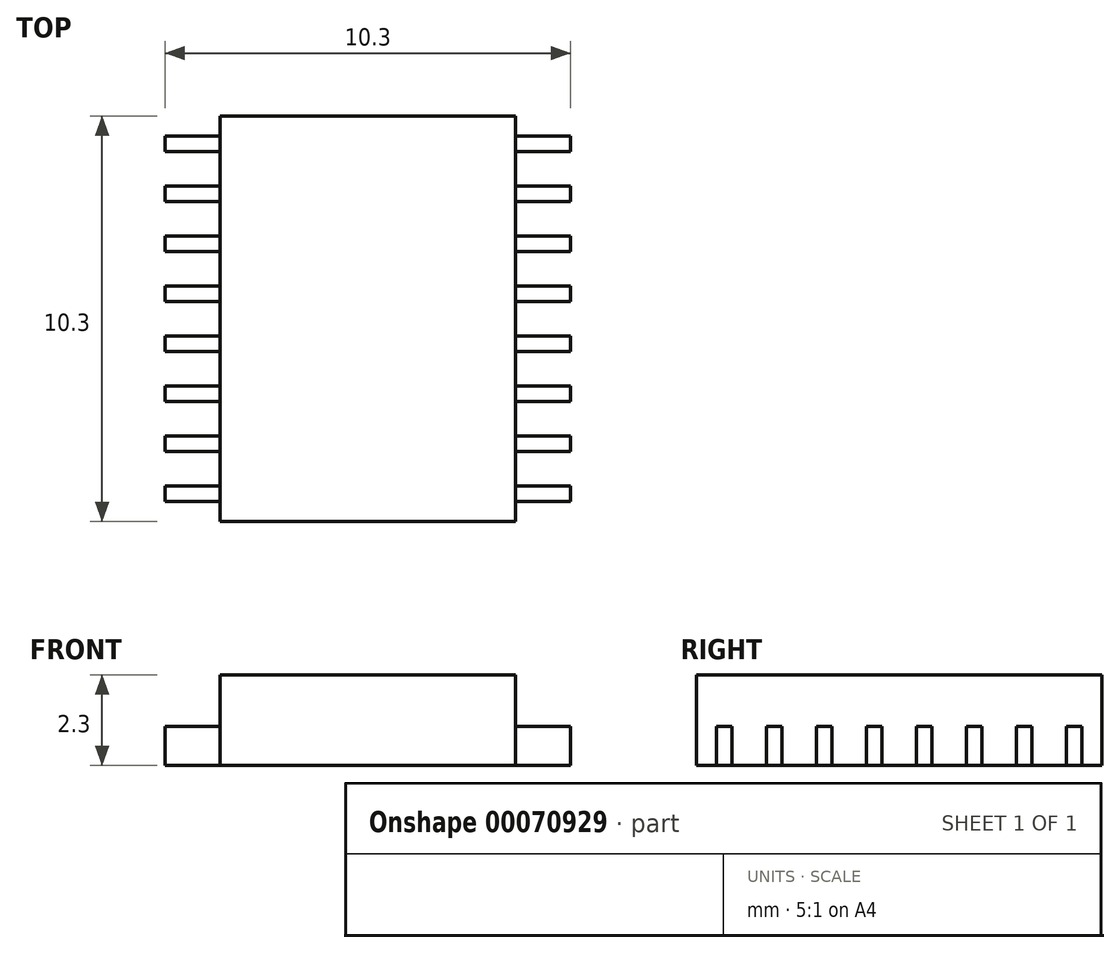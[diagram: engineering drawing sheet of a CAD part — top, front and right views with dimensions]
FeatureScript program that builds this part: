
annotation { "Feature Type Name" : "Feature", "Feature Type Description" : "" }
export const myFeature = defineFeature(function(context is Context, id is Id, definition is map)
    precondition{}
    {
        {
            var Q0;
            Q0=qCreatedBy(makeId("Top.planeOp"),FACE);
            var sketch = newSketch(context, id + "F0", { "sketchPlane" : qUnion([Q0])});
            skLineSegment(sketch, "E0.rect.bottom", {"start": v(3.75, -5.15) * mm, "end": v(-3.75, -5.15) * mm});
            skLineSegment(sketch, "E0.rect.top", {"start": v(3.75, 5.15) * mm, "end": v(-3.75, 5.15) * mm});
            skLineSegment(sketch, "E0.rect.left", {"start": v(3.75, -5.15) * mm, "end": v(3.75, 5.15) * mm});
            skLineSegment(sketch, "E0.rect.right", {"start": v(-3.75, -5.15) * mm, "end": v(-3.75, 5.15) * mm});
            skPoint(sketch, "E0.rect.middle", {"position": v(0, 0) * mm});
            skSolve(sketch);
        }
        {
            var Q0;
            Q0=qSketchRegion(id+"F0",true);
            extrude(context, id + "F1", {"entities" : qUnion([Q0]), "depth" : 2.3 * mm});
        }
        {
            var Q0;
            Q0=qCreatedBy(makeId("Top.planeOp"),FACE);
            var sketch = newSketch(context, id + "F2", { "sketchPlane" : qUnion([Q0])});
            skLineSegment(sketch, "E1.bottom", {"start": v(-3.75, 4.65) * mm, "end": v(-5.15, 4.65) * mm});
            skLineSegment(sketch, "E1.top", {"start": v(-3.75, 4.25) * mm, "end": v(-5.15, 4.25) * mm});
            skLineSegment(sketch, "E1.left", {"start": v(-3.75, 4.65) * mm, "end": v(-3.75, 4.25) * mm});
            skLineSegment(sketch, "E1.right", {"start": v(-5.15, 4.65) * mm, "end": v(-5.15, 4.25) * mm});
            skLineSegment(sketch, "E2.bottom", {"start": v(-5.15, 3.38) * mm, "end": v(-3.75, 3.38) * mm});
            skLineSegment(sketch, "E2.top", {"start": v(-5.15, 2.98) * mm, "end": v(-3.75, 2.98) * mm});
            skLineSegment(sketch, "E2.left", {"start": v(-5.15, 3.38) * mm, "end": v(-5.15, 2.98) * mm});
            skLineSegment(sketch, "E2.right", {"start": v(-3.75, 3.38) * mm, "end": v(-3.75, 2.98) * mm});
            skLineSegment(sketch, "E3.bottom", {"start": v(-5.15, 2.1) * mm, "end": v(-3.75, 2.1) * mm});
            skLineSegment(sketch, "E3.top", {"start": v(-5.15, 1.7) * mm, "end": v(-3.75, 1.7) * mm});
            skLineSegment(sketch, "E3.left", {"start": v(-5.15, 2.1) * mm, "end": v(-5.15, 1.7) * mm});
            skLineSegment(sketch, "E3.right", {"start": v(-3.75, 2.1) * mm, "end": v(-3.75, 1.7) * mm});
            skLineSegment(sketch, "E4.bottom", {"start": v(-5.15, -1.7) * mm, "end": v(-3.75, -1.7) * mm});
            skLineSegment(sketch, "E4.top", {"start": v(-5.15, -2.1) * mm, "end": v(-3.75, -2.1) * mm});
            skLineSegment(sketch, "E4.left", {"start": v(-5.15, -1.7) * mm, "end": v(-5.15, -2.1) * mm});
            skLineSegment(sketch, "E4.right", {"start": v(-3.75, -1.7) * mm, "end": v(-3.75, -2.1) * mm});
            skLineSegment(sketch, "E5.bottom", {"start": v(-5.15, 0.84) * mm, "end": v(-3.75, 0.84) * mm});
            skLineSegment(sketch, "E5.top", {"start": v(-5.15, 0.44) * mm, "end": v(-3.75, 0.44) * mm});
            skLineSegment(sketch, "E5.left", {"start": v(-5.15, 0.84) * mm, "end": v(-5.15, 0.43) * mm});
            skLineSegment(sketch, "E5.right", {"start": v(-3.75, 0.84) * mm, "end": v(-3.75, 0.44) * mm});
            skLineSegment(sketch, "E6.bottom", {"start": v(-5.15, -0.43) * mm, "end": v(-3.75, -0.43) * mm});
            skLineSegment(sketch, "E6.top", {"start": v(-5.15, -0.84) * mm, "end": v(-3.75, -0.84) * mm});
            skLineSegment(sketch, "E6.left", {"start": v(-5.15, -0.43) * mm, "end": v(-5.15, -0.84) * mm});
            skLineSegment(sketch, "E6.right", {"start": v(-3.75, -0.43) * mm, "end": v(-3.75, -0.83) * mm});
            skLineSegment(sketch, "E7.bottom", {"start": v(-5.15, -2.98) * mm, "end": v(-3.75, -2.98) * mm});
            skLineSegment(sketch, "E7.top", {"start": v(-5.15, -3.38) * mm, "end": v(-3.75, -3.38) * mm});
            skLineSegment(sketch, "E7.left", {"start": v(-5.15, -2.98) * mm, "end": v(-5.15, -3.38) * mm});
            skLineSegment(sketch, "E7.right", {"start": v(-3.75, -2.98) * mm, "end": v(-3.75, -3.38) * mm});
            skLineSegment(sketch, "E8.bottom", {"start": v(-5.15, -4.25) * mm, "end": v(-3.75, -4.25) * mm});
            skLineSegment(sketch, "E8.top", {"start": v(-5.15, -4.65) * mm, "end": v(-3.75, -4.65) * mm});
            skLineSegment(sketch, "E8.left", {"start": v(-5.15, -4.25) * mm, "end": v(-5.15, -4.65) * mm});
            skLineSegment(sketch, "E8.right", {"start": v(-3.75, -4.25) * mm, "end": v(-3.75, -4.64) * mm});
            skSolve(sketch);
        }
        {
            var Q0;
            Q0=qSketchRegion(id+"F2",true);
            extrude(context, id + "F3", {"entities" : qUnion([Q0]), "operationType" : NewBodyOperationType.ADD, "depth" : 1 * mm});
        }
        {
            var Q0;
            Q0=qCreatedBy(makeId("Front.planeOp"),FACE);
            var sketch = newSketch(context, id + "F4", { "sketchPlane" : qUnion([Q0])});
            skLineSegment(sketch, "E9", {"start": v(0, 0) * mm, "end": v(0, 9.6) * mm, "construction": true});
            skSolve(sketch);
        }
        {
            var Q0;
            Q0=makeQuery(id+"F1.opExtrude","SWEPT_BODY",BODY,{"disambiguationData":[OSD([sQuery(id+"F0.wireOp",EDGE,"E0.rect.bottom"),sQuery(id+"F0.wireOp",EDGE,"E0.rect.top"),sQuery(id+"F0.wireOp",EDGE,"E0.rect.left"),sQuery(id+"F0.wireOp",EDGE,"E0.rect.right")])]});
            var Q1;
            Q1=sQuery(id+"F4.wireOp",EDGE,"E9");
            circularPattern(context, id + "F5", {"operationType" : NewBodyOperationType.ADD, "entities" : qUnion([Q0]), "axis" : qUnion([Q1]), "angle" : 180 * degree, "instanceCount" : 2});
        }
    });
